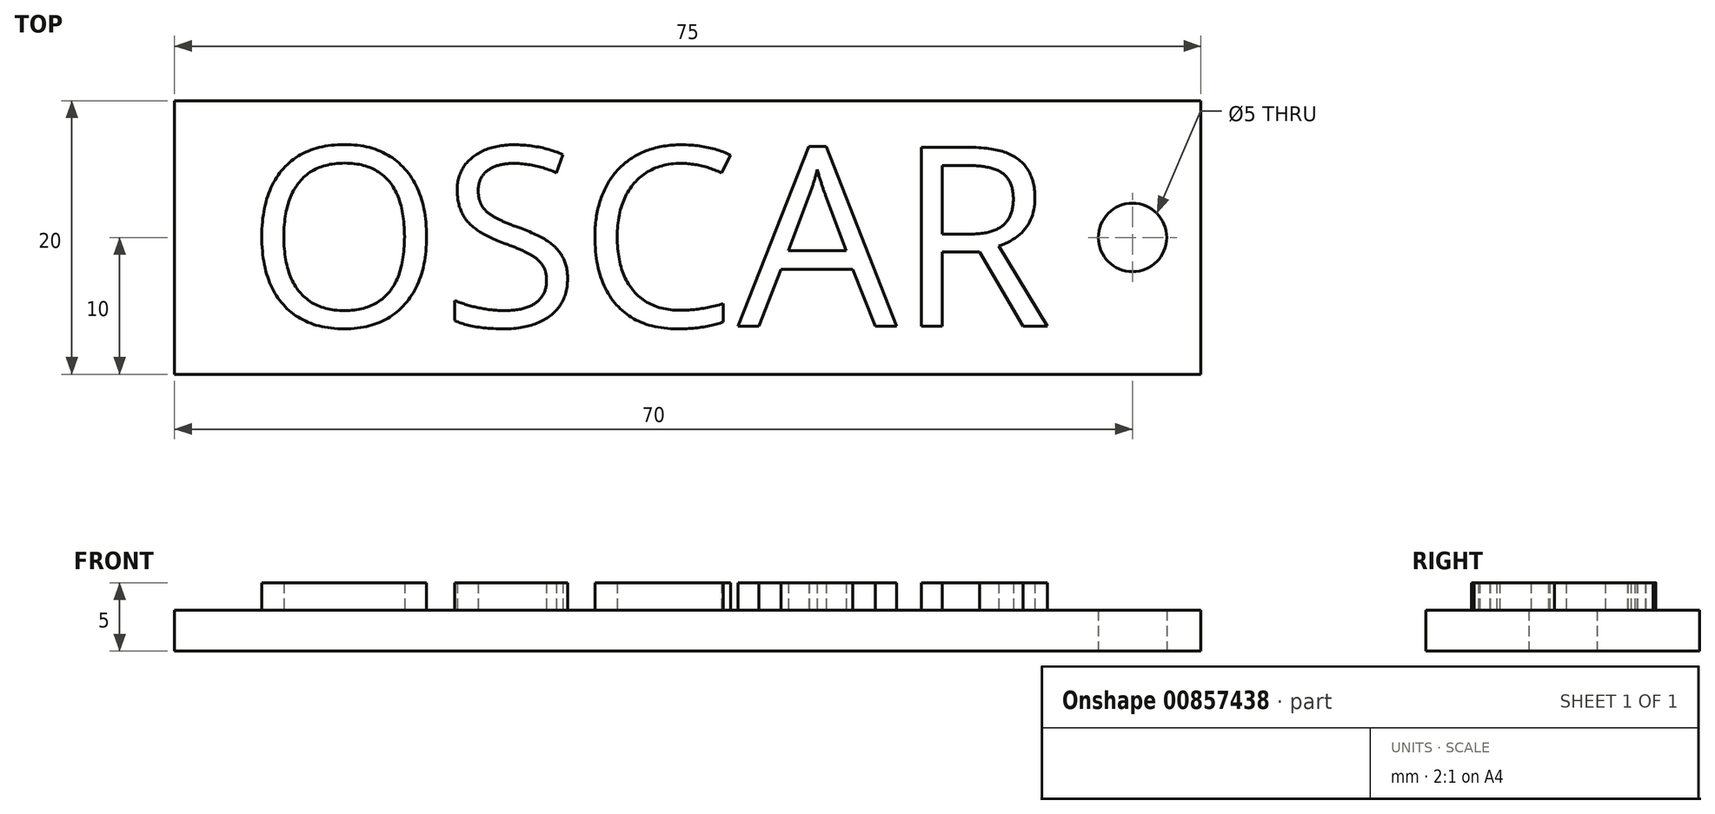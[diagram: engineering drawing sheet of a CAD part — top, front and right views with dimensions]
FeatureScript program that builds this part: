
annotation { "Feature Type Name" : "Feature", "Feature Type Description" : "" }
export const myFeature = defineFeature(function(context is Context, id is Id, definition is map)
    precondition{}
    {
        {
            var Q0;
            Q0=qCreatedBy(makeId("Top.planeOp"),FACE);
            var sketch = newSketch(context, id + "F0", { "sketchPlane" : qUnion([Q0])});
            skLineSegment(sketch, "E0.bottom", {"start": v(0, 0) * mm, "end": v(75, 0) * mm});
            skLineSegment(sketch, "E0.top", {"start": v(0, -20) * mm, "end": v(75, -20) * mm});
            skLineSegment(sketch, "E0.left", {"start": v(0, 0) * mm, "end": v(0, -20) * mm});
            skLineSegment(sketch, "E0.right", {"start": v(75, 0) * mm, "end": v(75, -20) * mm});
            skCircle(sketch, "E1", {"center": v(70, -10) * mm, "radius": 2.5 * mm});
            skSolve(sketch);
        }
        {
            var Q0;
            Q0=makeQuery(id+"F0.imprint","IMPRINT",FACE,{"disambiguationData":[TD([[makeQuery(id+"F0.imprint","IMPRINT",EDGE,{"derivedFrom":sQuery(id+"F0.wireOp",EDGE,"E0.bottom")}),-1.0]])]});
            extrude(context, id + "F1", {"entities" : qUnion([Q0]), "depth" : 3 * mm, "offsetDistance" : 25 * mm});
        }
        {
            var Q0;
            Q0=makeQuery(id+"F1.opExtrude","CAP_FACE",FACE,{"disambiguationData":[OSD([sQuery(id+"F0.wireOp",EDGE,"E0.bottom"),sQuery(id+"F0.wireOp",EDGE,"E0.top"),sQuery(id+"F0.wireOp",EDGE,"E0.left"),sQuery(id+"F0.wireOp",EDGE,"E0.right"),sQuery(id+"F0.wireOp",EDGE,"E1")])],"isStart":false});
            var sketch = newSketch(context, id + "F2", { "sketchPlane" : qUnion([Q0])});
            skText(sketch, "E2", { "text": "OSCAR", "fontName": "OpenSans-Regular.ttf"});
            const initialGuessF2  = {"E2": [0.00526, -0.0165, 1, 0, 0.0132]};
            skSetInitialGuess(sketch, initialGuessF2);
            skSolve(sketch);
        }
        {
            var Q0;
            Q0 = qSketchRegion(id + "F2", true);
            extrude(context, id + "F3", {"entities" : qUnion([Q0]), "operationType" : NewBodyOperationType.ADD, "depth" : 2 * mm, "offsetDistance" : 25 * mm});
        }
    });
